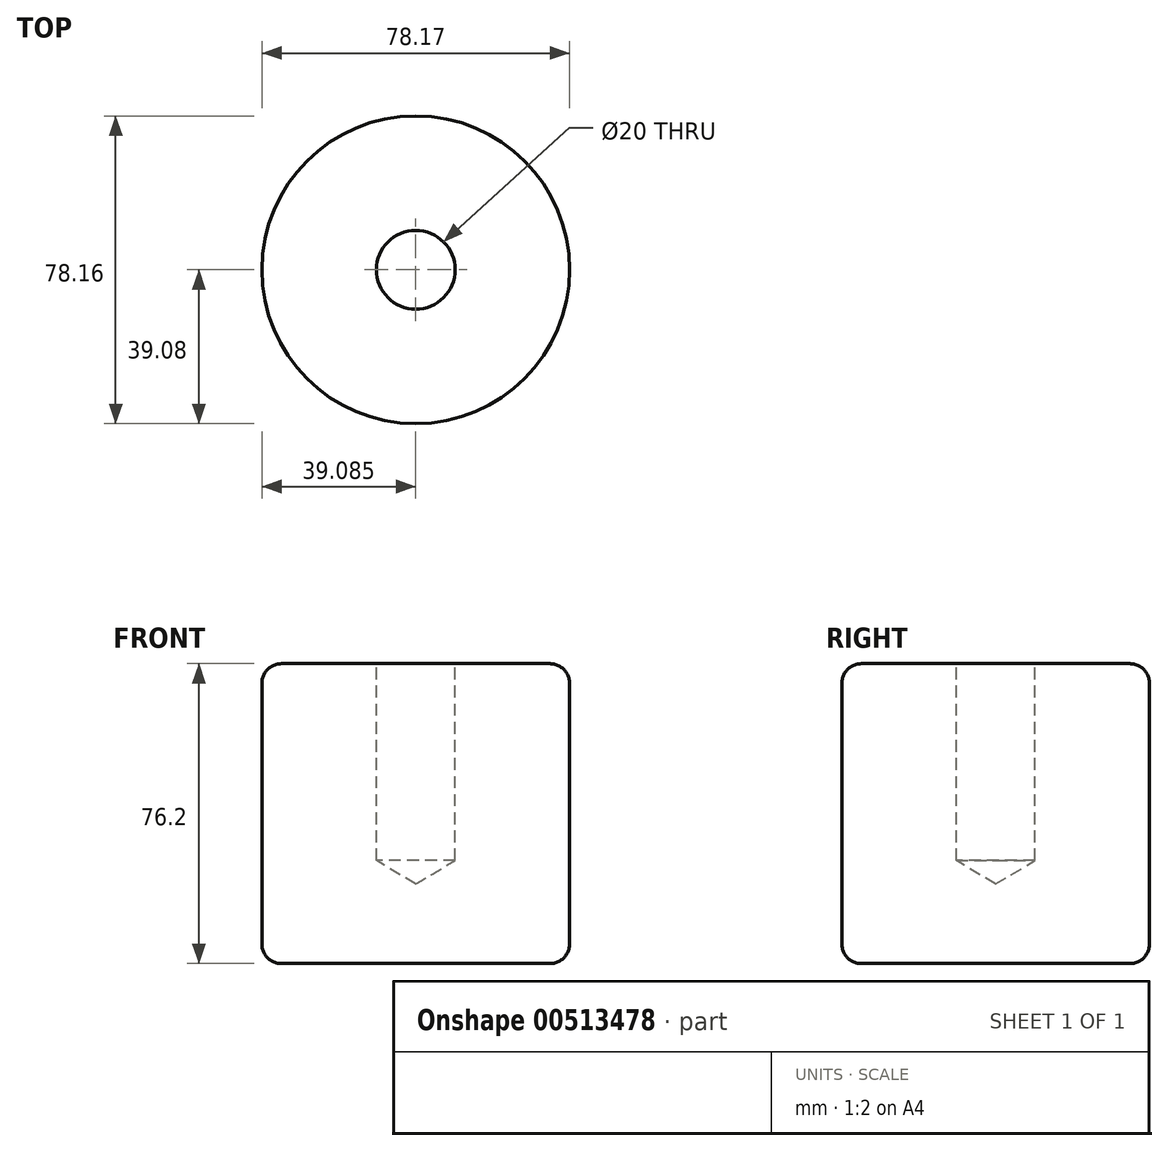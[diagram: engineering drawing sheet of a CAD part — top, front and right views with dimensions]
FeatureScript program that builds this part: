
annotation { "Feature Type Name" : "Feature", "Feature Type Description" : "" }
export const myFeature = defineFeature(function(context is Context, id is Id, definition is map)
    precondition{}
    {
        {
            var Q0;
            Q0=qCreatedBy(makeId("Top.planeOp"),FACE);
            var sketch = newSketch(context, id + "F0", { "sketchPlane" : qUnion([Q0])});
            skCircle(sketch, "E0", {"center": v(-14.6, 0) * mm, "radius": 39.08 * mm});
            skSolve(sketch);
        }
        {
            var Q0;
            Q0 = qSketchRegion(id + "F0", true);
            var Q1;
            Q1=makeQuery(id+"F0.imprint","IMPRINT",FACE,{"disambiguationData":[TD([[makeQuery(id+"F0.imprint","IMPRINT",EDGE,{"derivedFrom":sQuery(id+"F0.wireOp",EDGE,"E0")}),1.0]])]});
            extrude(context, id + "F1", {"entities" : qUnion([Q0, Q1]), "depth" : 76.2 * mm});
        }
        {
            var Q0;
            Q0=makeQuery(id+"F1.opExtrude","SWEPT_FACE",FACE,{"disambiguationData":[OSD([sQuery(id+"F0.wireOp",EDGE,"E0")])]});
            fillet(context, id + "F2", {"entities" : qUnion([Q0]), "radius" : 5 * mm, "tangentPropagation" : true, "allowEdgeOverflow" : false});
        }
        {
            var Q0;
            Q0=makeQuery(id+"F1.opExtrude","CAP_FACE",FACE,{"disambiguationData":[OSD([sQuery(id+"F0.wireOp",EDGE,"E0")])],"isStart":false});
            var sketch = newSketch(context, id + "F3", { "sketchPlane" : qUnion([Q0])});
            skCircle(sketch, "E1", {"center": v(-14.6, 0) * mm, "radius": 13.85 * mm});
            skSolve(sketch);
        }
        {
            var Q0;
            Q0=sQuery(id+"F3.wireOp",VERTEX,"E1.center");
            var Q1;
            Q1=makeQuery(id+"F1.opExtrude","SWEPT_BODY",BODY,{"disambiguationData":[OSD([sQuery(id+"F0.wireOp",EDGE,"E0")])]});
            hole(context, id + "F4", {"style" : HoleStyle.C_BORE, "endStyle" : HoleEndStyle.BLIND, "holeDiameter" : 20 * mm, "cBoreDiameter" : 20 * mm, "cBoreDepth" : 30 * mm, "holeDepth" : 50 * mm, "isTappedThrough" : true, "tappedDepth" : 12 * mm, "tapClearance" : 3, "startFromSketch" : true, "locations" : qUnion([Q0]), "scope" : qUnion([Q1])});
        }
    });
